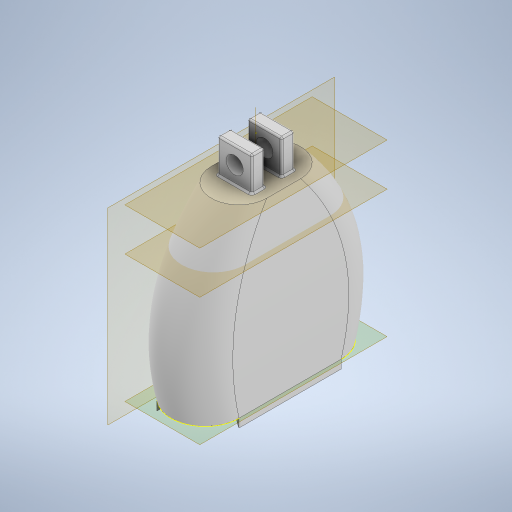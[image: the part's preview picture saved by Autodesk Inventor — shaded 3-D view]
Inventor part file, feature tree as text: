
AUTODESK INVENTOR PART (.ipt)
format: ipt  version: 2023 (Build 270158000, 158)  size: 586,240 bytes
history: native  units: mm
features: sketch x20, extrude x7, plane x4, fillet x2, chamfer x2, mirror x2, loft x1, shell x1, projected_geometry x1
ambient origin geometry x8: Origin, YZ Plane, XZ Plane, XY Plane, X Axis, Y Axis, Z Axis, Center Point
bodies: Solid1 (feature_tree)
feature tree (40):
  sketch  "Sketch1"  dims[d0=120.0mm d1=80.0mm d2=20.0mm]
  plane  "Work Plane1"
  sketch  "Sketch2"  dims[d3=200.0mm d4=40.0mm]
  plane  "Work Plane2"
  sketch  "Sketch3"  dims[d5=65.0mm d6=150.0mm]
  plane  "Work Plane3"
  loft  "Loft1"
  shell  "Shell1"  Thickness=20.0mm
  sketch  "Sketch4"  dims[d7=100.0mm d8=75.0mm]
  plane  "Work Plane4"
  extrude  "Extrusion1"  Depth=40.0mm
  sketch  "Sketch10"  dims[d15=3.0mm]
  extrude  "Extrusion2"  Depth=150.0mm
  sketch  "Sketch12"  dims[d22=40.0mm]
  extrude  "Extrusion3"  Depth=75.0mm
  extrude  "Extrusion4"  TaperAngle=0.0deg  [1 undecoded]
  fillet  "Fillet1"  [1 undecoded]
  chamfer  "Chamfer1"  Distance=10.0mm
  chamfer  "Chamfer2"  Distance=40.0mm
  extrude  "Extrusion5"  Depth=20.0mm TaperAngle=0.0deg
  extrude  "Extrusion7"  Depth=20.0mm TaperAngle=0.0deg
  mirror  "Mirror2"
  mirror  "Mirror3"
  sketch  "Sketch18"  dims[d36=2.0mm d37=2.0mm d38=45.0deg d39=55.0mm]
  sketch  "Sketch19"  dims[d40=25.0mm]
  extrude  "Extrusion8"  Depth=2.0mm TaperAngle=45.0deg
  fillet  "Fillet2"  Radius=55.0mm
  sketch  "Sketch21"  dims[d42=5.0mm]
  sketch  "Sketch22"  dims[d43=5.0mm]
  sketch  "Sketch23"  dims[d44=2.0mm]
  sketch  "Sketch24"  dims[d45=2.0mm]
  sketch  "Sketch25"  dims[d46=10.0mm d47=0.0mm d55=4.0mm d56=5.0mm d57=5.0mm d58=50.0mm d59=0.0mm d60=3.0mm d61=10.0mm d62=0.0mm d63=20.0mm]
  sketch  "Sketch9"  dims[d9=0.0mm d10=90.0deg d11=0.0mm d12=90.0deg d13=0.0mm d14=90.0deg]
  projected_geometry  "Projected Loop1"
  sketch  "Sketch11"  dims[d19=21.0mm d20=10.0mm d21=0.0mm]
  sketch  "Sketch13"  dims[d23=50.0mm d24=40.0mm d25=0.0mm]
  sketch  "Sketch14"  dims[d26=20.0mm d27=50.0mm d28=0.0mm]
  sketch  "Sketch15"  dims[d29=20.0mm d30=40.0mm d31=0.0mm]
  sketch  "Sketch17"  dims[d32=2.0mm d33=2.0mm d34=2.0mm d35=45.0deg]
  sketch  "Sketch20"  dims[d41=12.5mm]
note: 2 required parameter values undecoded (feature->parameter linkage not recoverable at this tier; creation-order binding heuristic only, values carry confidence <= 0.55)
